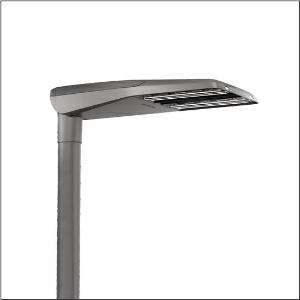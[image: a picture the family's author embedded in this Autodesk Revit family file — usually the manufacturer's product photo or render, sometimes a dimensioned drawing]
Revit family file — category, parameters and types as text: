
# Revit family: streetlight_sl_11_iq_midi___st1_2a_5xc3a41e08le_4284
name_source: partatom
category: Lighting Fixtures
units: mm (PartAtom-declared; Revit-internal decimal feet)

## family parameters
Cut with Voids When Loaded = No
Host = Face
Light Source = No
Part Type = Normal
Room Calculation Point = No
Round Connector Dimension = Use Diameter
Shared = No

## types (1)
- --- (1 x LED, 9590 lm, 60.4 W, 4000K)
    Apparent Load = 60 VA
    CIE Flux Codes = 32 70 96 100 100
    Color Rendering = 70
    Color Temperature = 4000K
    Default Elevation = 1800 mm
    Description = Streetlight SL 11 iQ midi, mast luminaire, primary light control with 3 zone facetted reflector, of plastic, silver coated, highly specular, primary optical cover: cover, of PMMA, transparent, light distribution: ST1.2a, light emission: direct distribution, primary light characteristic: asymmetric, installation type: post-top, side-entry, LED, High Power LED, rated luminous flux: 9.590lm, luminous efficacy: 159lm/W, light colour: 740, colour temperature: 4000K, control: optimised constant luminous flux control (CLO 2.0), Desk-Remote (wireless, voltage-free reading and setting of iQ features in the workshop via application-optimized NFC function/RFID function), Light-Fading, Smart-Wire, Night-Set, Lumen-Switch, Temp-Guard, Auto-Match, with cable H07RN-F 5x 1.5mm², mains connection: 230..240V, AC, 50/60Hz, connection cable pre-assembled, cable length: 8,5m, start of lifetime: 60W, end of service life: 63W, reduction: 30W, luminaire housing, of diecast aluminium, powder-coated, Siteco® metallic grey (DB 702S), please order mast flange separately, inclination adjustable without tools: 0°, 5°, 10°, 15° (post-top) | 0°, -5°, -10°, -15° (side-entry), sealing non-destructively replaceable, multi-level sealing system, length: 780mm, width: 376mm, height: 118mm, mast flange for spigot size: 42mm (side-entry): 5XC10008XM4, 60/48mm (side-entry/post-top): 5XC10108XM2, 76/60mm (side-entry/post-top): 5XC10108XM1, equipment: standard, protection rating (complete): IP66, insulation class (complete): insulation class II (safety insulation), certification: CE, ENEC, VDE, impact resistance: IK09, permissible operating ambient temperature for outdoor applications: -25..+50°C, standard-compliant lighting for roads and squares, Environmental Product Declaration (EPD) tested and certified by an independent institute, packaging unit: 1 piece

Light Distribution: ST1.2a
    Height = 118 mm
    Lamp = 1 x LED
    Lamp Light Flux = 9590 lm
    Lamp Power = 60.4 W
    Lamp count = 1
    Length = 780 mm
    Luminous efficacy = 159 lm/W
    Manufacturer = Siteco
    ModVariant = No
    Model = 5XC3A41E08LE
    Number of Poles = 1
    OnlyDefault = Yes
    Power Factor = 1
    Product Name = Streetlight SL 11 iQ midi | ST1.2a
    Product group = mast luminaire | pylon top
    ProductGroupID = 6100
    Protection Class = Protection class II
    Protection Degree = IP 66
    RLX_Detail_Level = 1
    RLX_Emergency_Light_Flux = 0 lm
    RLX_Emergency_Type = 0
    RLX_Emergency_Type_DB = No
    RlxData = <blob elided: 70541 chars, md5=ff6fb538>
    Socket = socket
    Standby Power = 0 W
    System Light Flux = 9590 lm
    System Power = 60 W
    Type Comments = factory setting: luminous flux: 100 % | dim-lin: 254 | 520 mA
    Type Image = l_1005960.jpg
    URL = http://relux.com
    VarID = @adj_132827
    Voltage = 0 V
    Weight = 0.00 kg
    Width = 376 mm

## geometry (parser evidence)
native form markers: Blend x4, Sweep x10
no freeform markers — native parametric forms only
